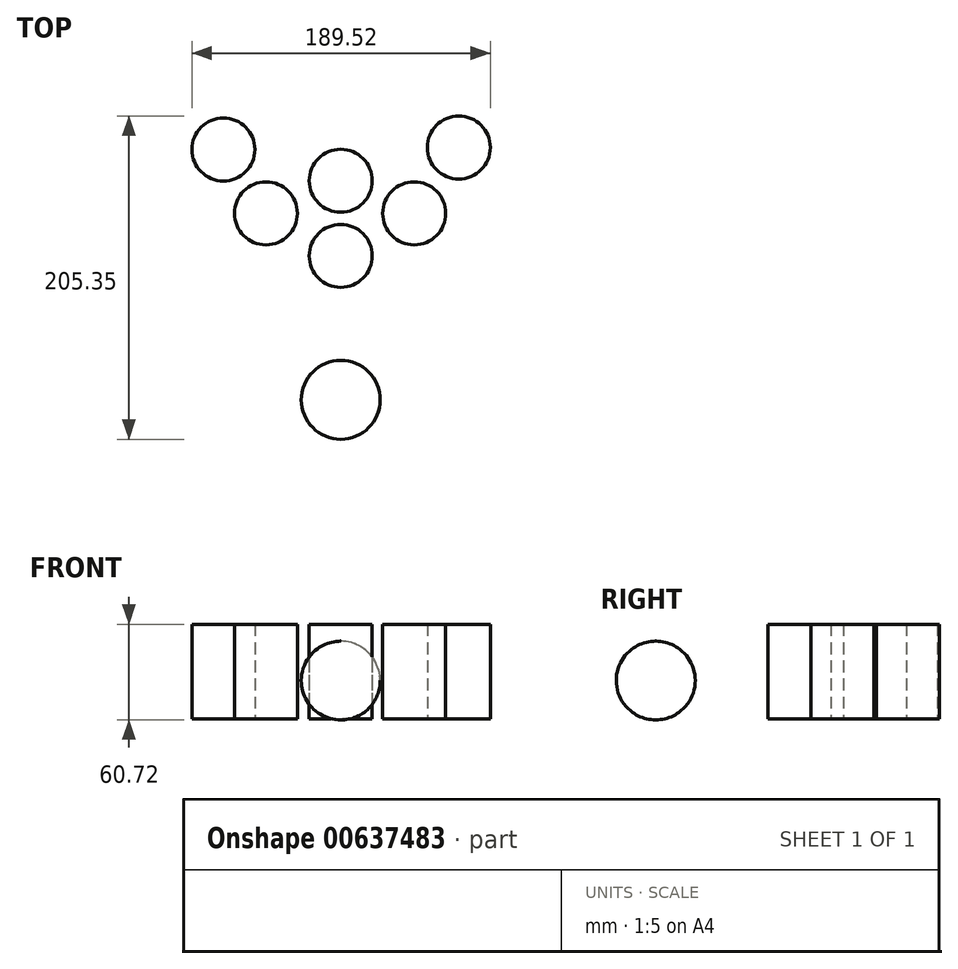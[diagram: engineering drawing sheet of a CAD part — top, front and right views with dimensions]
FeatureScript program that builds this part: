
annotation { "Feature Type Name" : "Feature", "Feature Type Description" : "" }
export const myFeature = defineFeature(function(context is Context, id is Id, definition is map)
    precondition{}
    {
        {
            var Q0;
            Q0=qCreatedBy(makeId("Right.planeOp"),FACE);
            var sketch = newSketch(context, id + "F0", { "sketchPlane" : qUnion([Q0])});
            skLineSegment(sketch, "E0", {"start": v(-98.26, 49.28) * mm, "end": v(-98.26, -0.72) * mm});
            skArc(sketch, "E1", {"start": v(-98.26, 49.28) * mm, "mid": v(-123.34, 24.28) * mm, "end": v(-98.26, -0.72) * mm});
            skSolve(sketch);
        }
        {
            var Q0;
            Q0=makeQuery(id+"F0.imprint","IMPRINT",FACE,{"disambiguationData":[TD([[makeQuery(id+"F0.imprint","IMPRINT",EDGE,{"derivedFrom":sQuery(id+"F0.wireOp",EDGE,"E0")}),-1.0]])]});
            var Q1;
            Q1=sQuery(id+"F0.wireOp",EDGE,"E0");
            revolve(context, id + "F1", {"entities" : qUnion([Q0]), "axis" : qUnion([Q1]), "revolveType" : RevolveType.FULL});
        }
        {
            var Q0;
            Q0=qCreatedBy(makeId("Top.planeOp"),FACE);
            var sketch = newSketch(context, id + "F2", { "sketchPlane" : qUnion([Q0])});
            skCircle(sketch, "E2", {"center": v(0, -6.84) * mm, "radius": 20 * mm});
            skCircle(sketch, "E3", {"center": v(-47.52, 20.2) * mm, "radius": 20 * mm});
            skCircle(sketch, "E4", {"center": v(46.67, 20.2) * mm, "radius": 20 * mm});
            skCircle(sketch, "E5", {"center": v(-74.55, 60.74) * mm, "radius": 20 * mm});
            skCircle(sketch, "E6", {"center": v(74.97, 62) * mm, "radius": 20 * mm});
            skCircle(sketch, "E7", {"center": v(0, 40.89) * mm, "radius": 20 * mm});
            skSolve(sketch);
        }
        {
            var Q0;
            Q0=makeQuery(id+"F2.imprint","IMPRINT",FACE,{"disambiguationData":[TD([[makeQuery(id+"F2.imprint","IMPRINT",EDGE,{"derivedFrom":sQuery(id+"F2.wireOp",EDGE,"E5")}),1.0]])]});
            var Q1;
            Q1=makeQuery(id+"F2.imprint","IMPRINT",FACE,{"disambiguationData":[TD([[makeQuery(id+"F2.imprint","IMPRINT",EDGE,{"derivedFrom":sQuery(id+"F2.wireOp",EDGE,"E3")}),1.0]])]});
            var Q2;
            Q2=makeQuery(id+"F2.imprint","IMPRINT",FACE,{"disambiguationData":[TD([[makeQuery(id+"F2.imprint","IMPRINT",EDGE,{"derivedFrom":sQuery(id+"F2.wireOp",EDGE,"E2")}),1.0]])]});
            var Q3;
            Q3=makeQuery(id+"F2.imprint","IMPRINT",FACE,{"disambiguationData":[TD([[makeQuery(id+"F2.imprint","IMPRINT",EDGE,{"derivedFrom":sQuery(id+"F2.wireOp",EDGE,"E7")}),1.0]])]});
            var Q4;
            Q4=makeQuery(id+"F2.imprint","IMPRINT",FACE,{"disambiguationData":[TD([[makeQuery(id+"F2.imprint","IMPRINT",EDGE,{"derivedFrom":sQuery(id+"F2.wireOp",EDGE,"E4")}),1.0]])]});
            var Q5;
            Q5=makeQuery(id+"F2.imprint","IMPRINT",FACE,{"disambiguationData":[TD([[makeQuery(id+"F2.imprint","IMPRINT",EDGE,{"derivedFrom":sQuery(id+"F2.wireOp",EDGE,"E6")}),1.0]])]});
            extrude(context, id + "F3", {"entities" : qUnion([Q0, Q1, Q2, Q3, Q4, Q5]), "depth" : 60 * mm, "offsetDistance" : 25 * mm});
        }
    });
